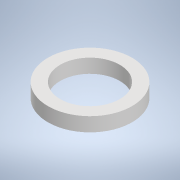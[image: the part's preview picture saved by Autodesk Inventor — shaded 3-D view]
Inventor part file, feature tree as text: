
AUTODESK INVENTOR PART (.ipt)
format: ipt  version: 2022 (Build 260153070, 153G)  size: 100,352 bytes
history: native  units: mm
features: extrude x1, sketch x1
ambient origin geometry x8: Origin, YZ Plane, XZ Plane, XY Plane, X Axis, Y Axis, Z Axis, Center Point
bodies: Solid1 (feature_tree)
feature tree (2):
  extrude  "Extrusion1"  Depth=4.0mm
  sketch  "Sketch1"  dims[d0=17.0mm d1=23.0mm d2=4.0mm d3=0.0mm]
